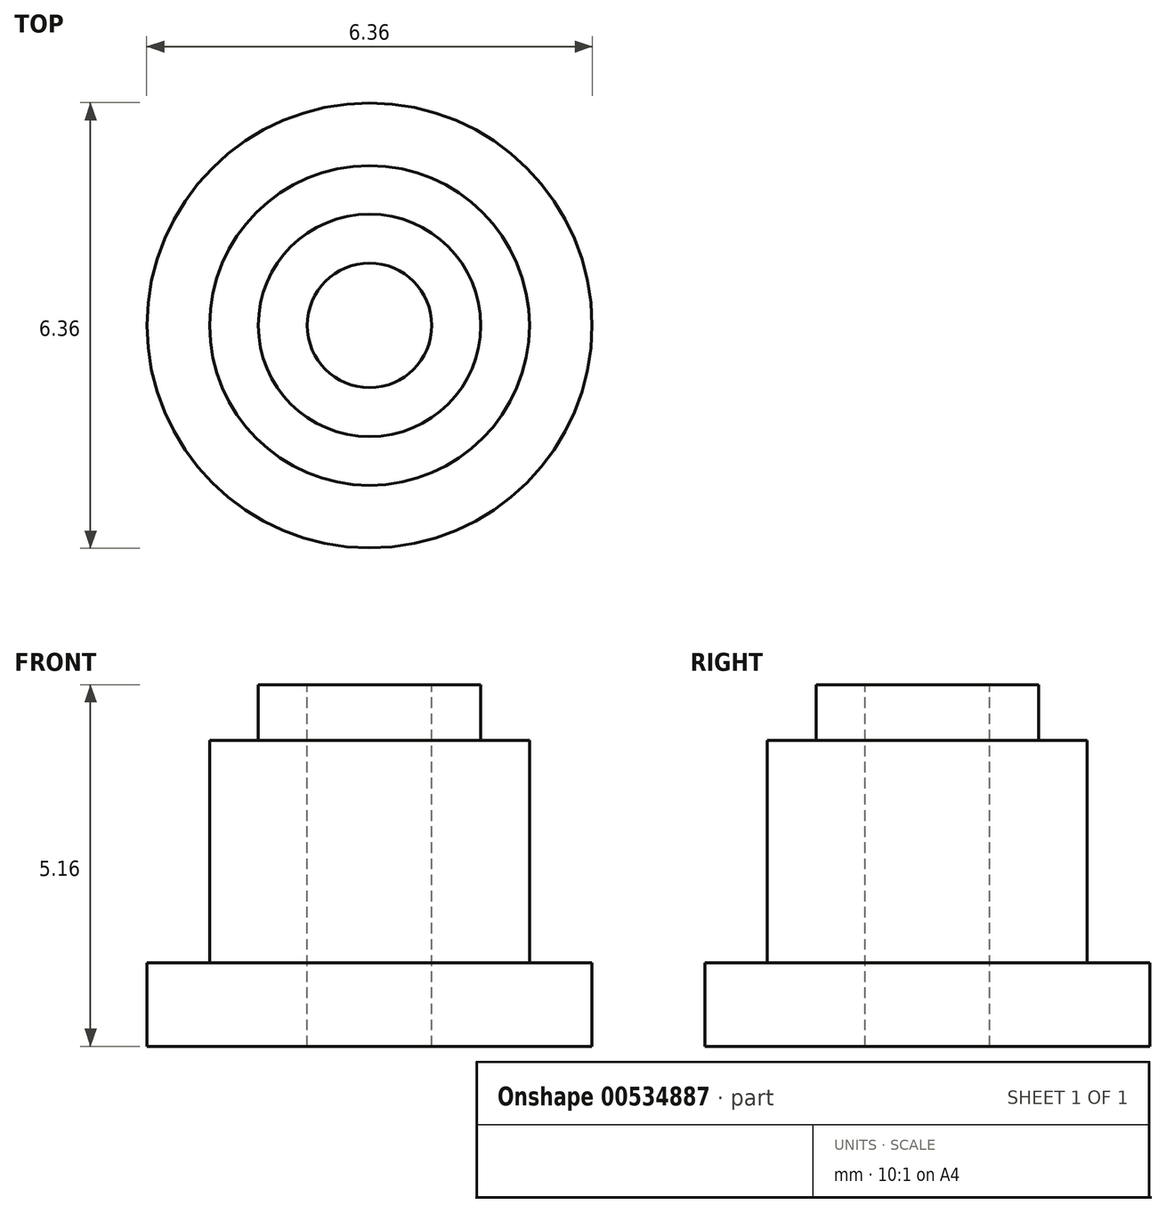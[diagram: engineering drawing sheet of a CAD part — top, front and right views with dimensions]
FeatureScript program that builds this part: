
annotation { "Feature Type Name" : "Feature", "Feature Type Description" : "" }
export const myFeature = defineFeature(function(context is Context, id is Id, definition is map)
    precondition{}
    {
        {
            var Q0;
            Q0=qCreatedBy(makeId("Top.planeOp"),FACE);
            var sketch = newSketch(context, id + "F0", { "sketchPlane" : qUnion([Q0])});
            skCircle(sketch, "E0", {"center": v(0, 0) * mm, "radius": 3.18 * mm});
            skSolve(sketch);
        }
        {
            var Q0;
            Q0 = qSketchRegion(id + "F0", true);
            extrude(context, id + "F1", {"entities" : qUnion([Q0]), "depth" : 1.2 * mm, "offsetDistance" : 25.4 * mm});
        }
        {
            var Q0;
            Q0=makeQuery(id+"F1.opExtrude","CAP_FACE",FACE,{"disambiguationData":[OSD([sQuery(id+"F0.wireOp",EDGE,"E0")])],"isStart":false});
            var sketch = newSketch(context, id + "F2", { "sketchPlane" : qUnion([Q0])});
            skCircle(sketch, "E1", {"center": v(0, 0) * mm, "radius": 2.28 * mm});
            skSolve(sketch);
        }
        {
            var Q0;
            Q0 = qSketchRegion(id + "F2", true);
            extrude(context, id + "F3", {"entities" : qUnion([Q0]), "operationType" : NewBodyOperationType.ADD, "depth" : 3.17 * mm, "offsetDistance" : 25.4 * mm});
        }
        {
            var Q0;
            Q0=makeQuery(id+"F3.opExtrude","CAP_FACE",FACE,{"disambiguationData":[OSD([sQuery(id+"F2.wireOp",EDGE,"E1")])],"isStart":false});
            var sketch = newSketch(context, id + "F4", { "sketchPlane" : qUnion([Q0])});
            skCircle(sketch, "E2", {"center": v(0, 0) * mm, "radius": 1.59 * mm});
            skSolve(sketch);
        }
        {
            var Q0;
            Q0 = qSketchRegion(id + "F4", true);
            extrude(context, id + "F5", {"entities" : qUnion([Q0]), "operationType" : NewBodyOperationType.ADD, "depth" : 0.8 * mm, "offsetDistance" : 25.4 * mm});
        }
        {
            var Q0;
            Q0=makeQuery(id+"F5.opExtrude","CAP_FACE",FACE,{"disambiguationData":[OSD([sQuery(id+"F4.wireOp",EDGE,"E2")])],"isStart":false});
            var sketch = newSketch(context, id + "F6", { "sketchPlane" : qUnion([Q0])});
            skCircle(sketch, "E3", {"center": v(0, 0) * mm, "radius": 0.89 * mm});
            skSolve(sketch);
        }
        {
            var Q0;
            Q0 = qSketchRegion(id + "F6", true);
            extrude(context, id + "F7", {"entities" : qUnion([Q0]), "operationType" : NewBodyOperationType.REMOVE, "endBound" : BoundingType.THROUGH_ALL, "oppositeDirection" : true, "depth" : 25.4 * mm, "offsetDistance" : 25.4 * mm});
        }
    });
